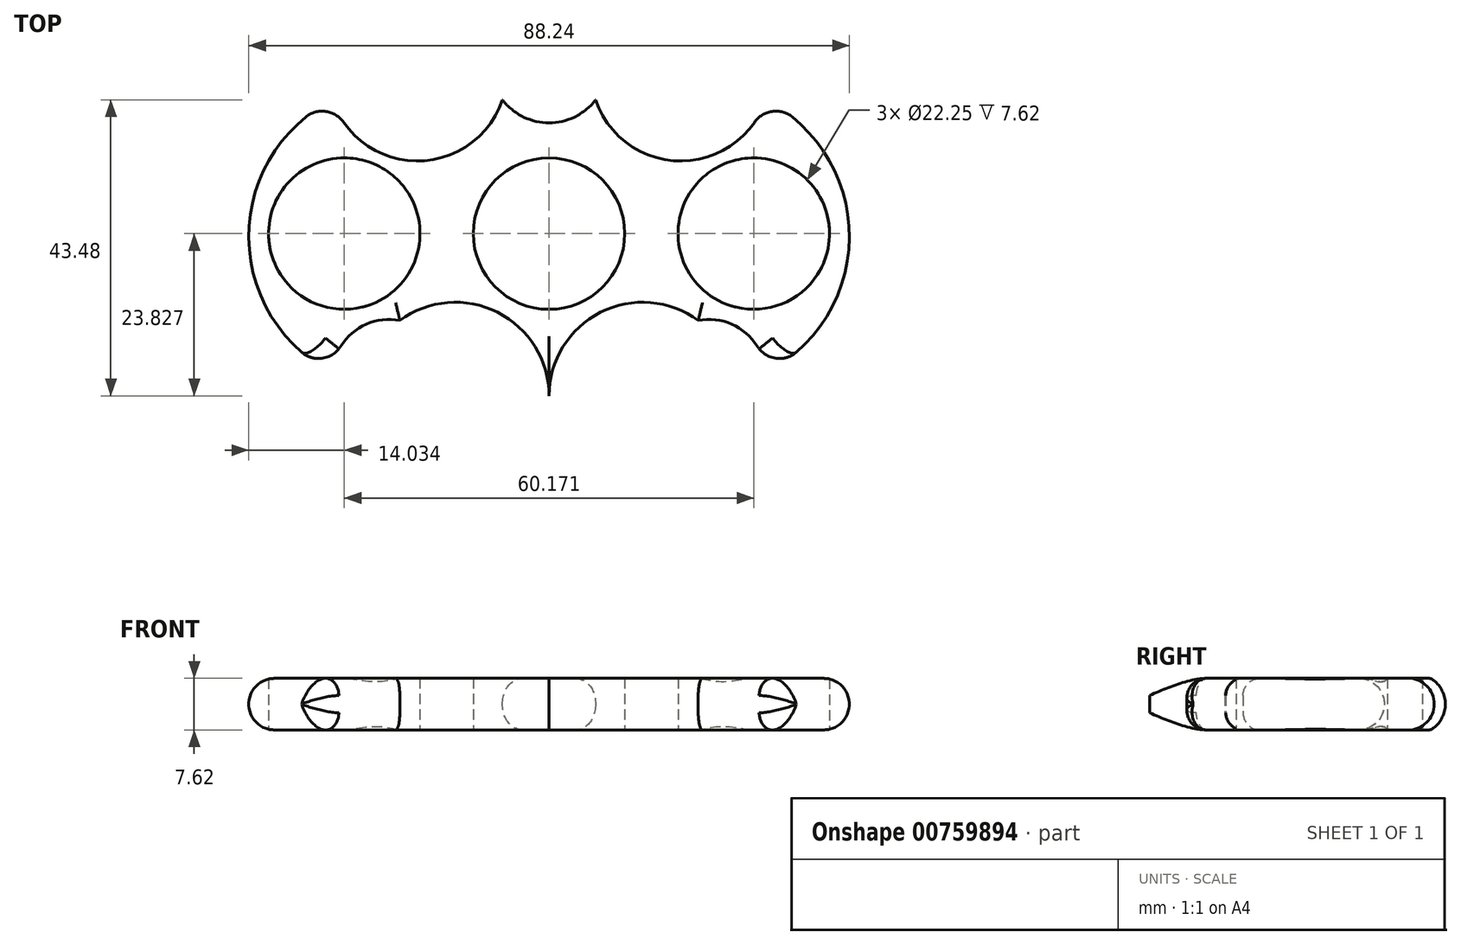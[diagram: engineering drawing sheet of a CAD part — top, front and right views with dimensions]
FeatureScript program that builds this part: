
annotation { "Feature Type Name" : "Feature", "Feature Type Description" : "" }
export const myFeature = defineFeature(function(context is Context, id is Id, definition is map)
    precondition{}
    {
        {
            var Q0;
            Q0=qCreatedBy(makeId("Top.planeOp"),FACE);
            var sketch = newSketch(context, id + "F0", { "sketchPlane" : qUnion([Q0])});
            skArc(sketch, "E0", {"start": v(-31.85, 32.42) * mm, "mid": v(-19.35, 23.44) * mm, "end": v(-6.84, 32.42) * mm});
            skArc(sketch, "E1", {"start": v(-31.85, 32.42) * mm, "mid": v(-44.12, 12.37) * mm, "end": v(-31.85, -7.68) * mm});
            skArc(sketch, "E2", {"start": v(-21.93, 0) * mm, "mid": v(-28.63, -1.6) * mm, "end": v(-31.85, -7.68) * mm});
            skArc(sketch, "E3.MirrorCS", {"start": v(31.85, 32.42) * mm, "mid": v(19.35, 23.44) * mm, "end": v(6.84, 32.42) * mm});
            skArc(sketch, "E4.MirrorCS", {"start": v(31.85, 32.42) * mm, "mid": v(44.12, 12.37) * mm, "end": v(31.85, -7.68) * mm});
            skArc(sketch, "E5.MirrorCS", {"start": v(21.93, 0) * mm, "mid": v(28.63, -1.6) * mm, "end": v(31.85, -7.68) * mm});
            skArc(sketch, "E6", {"start": v(-6.84, 32.42) * mm, "mid": v(0, 29.05) * mm, "end": v(6.84, 32.42) * mm});
            skArc(sketch, "E7", {"start": v(0, -11.06) * mm, "mid": v(-7.56, 1.2) * mm, "end": v(-21.93, 0) * mm});
            skArc(sketch, "E8.MirrorCS", {"start": v(0, -11.06) * mm, "mid": v(7.56, 1.2) * mm, "end": v(21.93, 0) * mm});
            skCircle(sketch, "E9", {"center": v(-30.09, 12.77) * mm, "radius": 11.13 * mm});
            skCircle(sketch, "E10.MirrorC", {"center": v(30.09, 12.77) * mm, "radius": 11.13 * mm});
            skCircle(sketch, "E11", {"center": v(0, 12.77) * mm, "radius": 11.13 * mm});
            skSolve(sketch);
        }
        {
            var Q0;
            Q0=makeQuery(id+"F0.imprint","IMPRINT",FACE,{"disambiguationData":[TD([[makeQuery(id+"F0.imprint","IMPRINT",EDGE,{"derivedFrom":sQuery(id+"F0.wireOp",EDGE,"E0")}),-1.0]])]});
            extrude(context, id + "F1", {"entities" : qUnion([Q0]), "endBound" : BoundingType.SYMMETRIC, "depth" : 7.62 * mm, "offsetDistance" : 25.4 * mm});
        }
        {
            var Q0;
            Q0=makeQuery(id+"F1.opExtrude","CAP_EDGE",EDGE,{"disambiguationData":[OSD([sQuery(id+"F0.wireOp",EDGE,"E3.MirrorCS")])],"isStart":true});
            var Q1;
            Q1=makeQuery(id+"F1.opExtrude","CAP_EDGE",EDGE,{"disambiguationData":[OSD([sQuery(id+"F0.wireOp",EDGE,"E3.MirrorCS")])],"isStart":false});
            var Q2;
            Q2=makeQuery(id+"F1.opExtrude","CAP_EDGE",EDGE,{"disambiguationData":[OSD([sQuery(id+"F0.wireOp",EDGE,"E0")])],"isStart":false});
            var Q3;
            Q3=makeQuery(id+"F1.opExtrude","CAP_EDGE",EDGE,{"disambiguationData":[OSD([sQuery(id+"F0.wireOp",EDGE,"E0")])],"isStart":true});
            fillet(context, id + "F2", {"entities" : qUnion([Q0, Q1, Q2, Q3]), "radius" : 3.8 * mm, "tangentPropagation" : true, "allowEdgeOverflow" : false});
        }
        {
            var Q0;
            Q0=makeQuery(id+"F1.opExtrude","CAP_EDGE",EDGE,{"disambiguationData":[OSD([sQuery(id+"F0.wireOp",EDGE,"E8.MirrorCS")])],"isStart":true});
            var Q1;
            Q1=makeQuery(id+"F1.opExtrude","CAP_EDGE",EDGE,{"disambiguationData":[OSD([sQuery(id+"F0.wireOp",EDGE,"E8.MirrorCS")])],"isStart":false});
            var Q2;
            Q2=makeQuery(id+"F1.opExtrude","CAP_EDGE",EDGE,{"disambiguationData":[OSD([sQuery(id+"F0.wireOp",EDGE,"E7")])],"isStart":true});
            var Q3;
            Q3=makeQuery(id+"F1.opExtrude","CAP_EDGE",EDGE,{"disambiguationData":[OSD([sQuery(id+"F0.wireOp",EDGE,"E7")])],"isStart":false});
            var Q4;
            Q4=makeQuery(id+"F1.opExtrude","CAP_EDGE",EDGE,{"disambiguationData":[OSD([sQuery(id+"F0.wireOp",EDGE,"E2")])],"isStart":true});
            var Q5;
            Q5=makeQuery(id+"F1.opExtrude","CAP_EDGE",EDGE,{"disambiguationData":[OSD([sQuery(id+"F0.wireOp",EDGE,"E2")])],"isStart":false});
            var Q6;
            Q6=makeQuery(id+"F1.opExtrude","CAP_EDGE",EDGE,{"disambiguationData":[OSD([sQuery(id+"F0.wireOp",EDGE,"E5.MirrorCS")])],"isStart":true});
            var Q7;
            Q7=makeQuery(id+"F1.opExtrude","CAP_EDGE",EDGE,{"disambiguationData":[OSD([sQuery(id+"F0.wireOp",EDGE,"E5.MirrorCS")])],"isStart":false});
            fillet(context, id + "F3", {"entities" : qUnion([Q0, Q1, Q2, Q3, Q4, Q5, Q6, Q7]), "radius" : 2.54 * mm, "tangentPropagation" : true, "allowEdgeOverflow" : false});
        }
        {
            var Q0;
            Q0=makeQuery(id+"F1.opExtrude","CAP_EDGE",EDGE,{"disambiguationData":[OSD([sQuery(id+"F0.wireOp",EDGE,"E4.MirrorCS")])],"isStart":true});
            var Q1;
            Q1=makeQuery(id+"F1.opExtrude","CAP_EDGE",EDGE,{"disambiguationData":[OSD([sQuery(id+"F0.wireOp",EDGE,"E4.MirrorCS")])],"isStart":false});
            var Q2;
            Q2=makeQuery(id+"F1.opExtrude","CAP_EDGE",EDGE,{"disambiguationData":[OSD([sQuery(id+"F0.wireOp",EDGE,"E1")])],"isStart":true});
            var Q3;
            Q3=makeQuery(id+"F1.opExtrude","CAP_EDGE",EDGE,{"disambiguationData":[OSD([sQuery(id+"F0.wireOp",EDGE,"E1")])],"isStart":false});
            fillet(context, id + "F4", {"entities" : qUnion([Q0, Q1, Q2, Q3]), "radius" : 3.8 * mm, "tangentPropagation" : true, "allowEdgeOverflow" : false});
        }
    });
